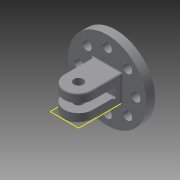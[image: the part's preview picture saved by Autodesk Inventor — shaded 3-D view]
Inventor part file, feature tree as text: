
AUTODESK INVENTOR PART (.ipt)
format: ipt  version: 2013 (Build 170138000, 138)  size: 192,512 bytes
history: native  units: mm
features: sketch x7, extrude x4, fillet x3, hole x2
ambient origin geometry x8: Origin, YZ Plane, XZ Plane, XY Plane, X Axis, Y Axis, Z Axis, Center Point
bodies: Solid1 (feature_tree)
feature tree (16):
  extrude  "Extrusion1"  Depth=6.0mm TaperAngle=0.0deg
  hole  "Hole1"  [1 undecoded]
  extrude  "Extrusion3"  Depth=18.0mm
  sketch  "Sketch9"  dims[d31=30.0mm d32=0.0mm d35=10.0mm]
  sketch  "Sketch10"  dims[d36=6.6mm d37=6.0mm d38=12.6mm d39=2.0mm d40=90.0deg d41=8.0mm d42=20.594885mm d43=25.0mm d44=0.0mm]
  fillet  "Fillet2"  Radius=20.0mm
  hole  "Hole3"  [1 undecoded]
  extrude  "Extrusion4"  Depth=25.0mm TaperAngle=0.0deg
  extrude  "Extrusion5"  TaperAngle=180.0deg  [1 undecoded]
  fillet  "Fillet3"  Radius=1.0mm
  fillet  "Fillet4"  [1 undecoded]
  sketch  "Sketch1"  dims[d0=55.0mm d1=6.0mm d2=0.0mm]
  sketch  "Sketch2"  dims[d3=20.0mm d4=80.0mm d6=360.0deg]
  sketch  "Sketch8"  dims[d8=6.6mm d9=6.0mm d10=12.6mm d11=2.0mm d12=90.0deg d13=8.0mm d14=20.594885mm d28=18.0mm d30=20.0mm]
  sketch  "Sketch11"  dims[d45=1.0mm d46=180.0deg d47=1.0mm d48=180.0deg]
  sketch  "Sketch12"  dims[d49=25.0mm d50=0.0mm d51=1.0mm d52=1.0mm d54=6.0mm]
note: 4 required parameter values undecoded (feature->parameter linkage not recoverable at this tier; creation-order binding heuristic only, values carry confidence <= 0.55)
